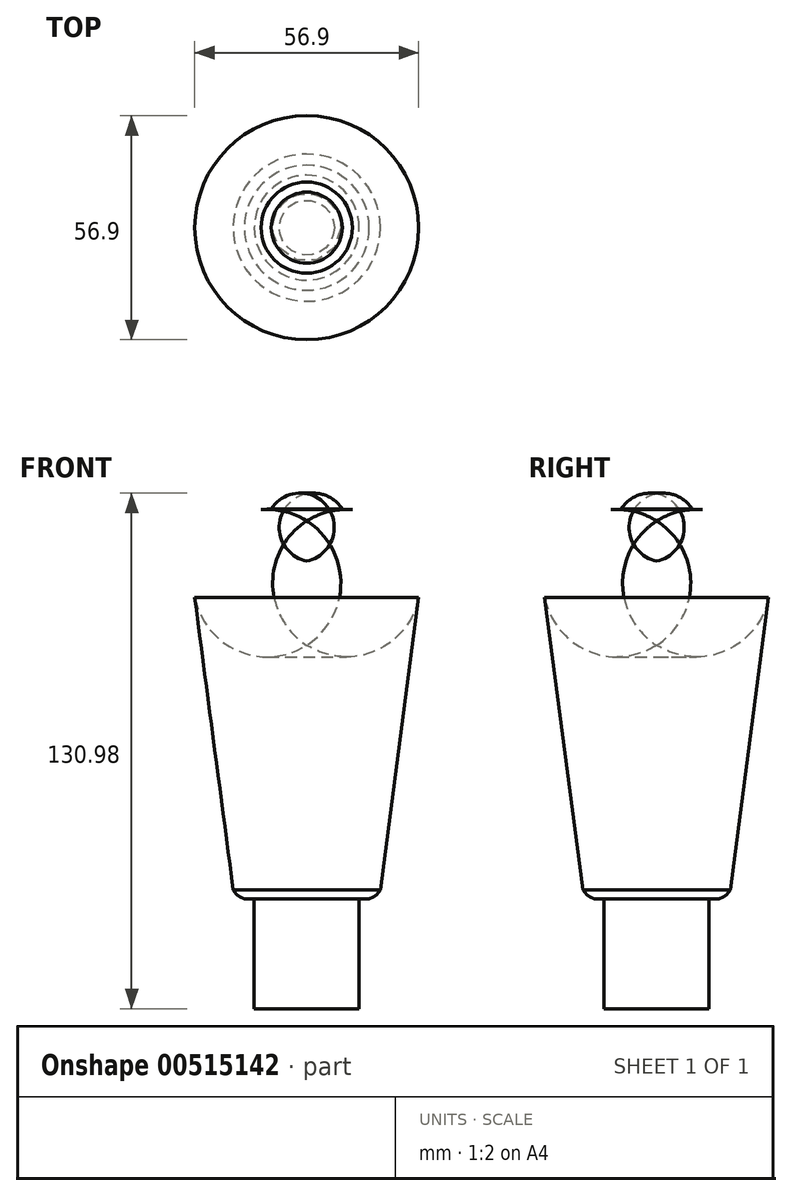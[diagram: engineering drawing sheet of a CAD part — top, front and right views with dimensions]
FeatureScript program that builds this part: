
annotation { "Feature Type Name" : "Feature", "Feature Type Description" : "" }
export const myFeature = defineFeature(function(context is Context, id is Id, definition is map)
    precondition{}
    {
        {
            var Q0;
            Q0=qCreatedBy(makeId("Front.planeOp"),FACE);
            var sketch = newSketch(context, id + "F0", { "sketchPlane" : qUnion([Q0])});
            skLineSegment(sketch, "E0", {"start": v(0, 0) * mm, "end": v(0, 130.8) * mm});
            skLineSegment(sketch, "E1.bottom", {"start": v(0, 0) * mm, "end": v(13.34, 0) * mm});
            skLineSegment(sketch, "E1.left", {"start": v(0, 0) * mm, "end": v(0, 27.94) * mm});
            skLineSegment(sketch, "E1.right", {"start": v(13.34, 0) * mm, "end": v(13.33, 27.94) * mm});
            skPoint(sketch, "E2.center.orphan", {"position": v(0, 91.69) * mm});
            skArc(sketch, "E3", {"start": v(28.45, 104.48) * mm, "mid": v(25, 119.41) * mm, "end": v(11.57, 126.78) * mm});
            skLineSegment(sketch, "E4", {"start": v(9.02, 126.98) * mm, "end": v(11.57, 126.78) * mm});
            skArc(sketch, "E5", {"start": v(9.02, 126.98) * mm, "mid": v(5.1, 130.29) * mm, "end": v(0, 130.8) * mm});
            skPoint(sketch, "E6.orphan", {"position": v(6.47, 127.19) * mm});
            skLineSegment(sketch, "E7", {"start": v(13.33, 27.94) * mm, "end": v(15.88, 27.94) * mm});
            skLineSegment(sketch, "E8", {"start": v(18.7, 30.17) * mm, "end": v(28.45, 104.48) * mm});
            skArc(sketch, "E9", {"start": v(15.88, 27.94) * mm, "mid": v(17.5, 28.8) * mm, "end": v(18.7, 30.17) * mm});
            skPoint(sketch, "E10.orphan", {"position": v(18.41, 27.94) * mm});
            skSolve(sketch);
        }
        {
            var Q0;
            Q0 = qSketchRegion(id + "F0", true);
            var Q1;
            Q1=sQuery(id+"F0.wireOp",EDGE,"E0");
            revolve(context, id + "F1", {"entities" : qUnion([Q0]), "axis" : qUnion([Q1]), "revolveType" : RevolveType.FULL});
        }
    });
